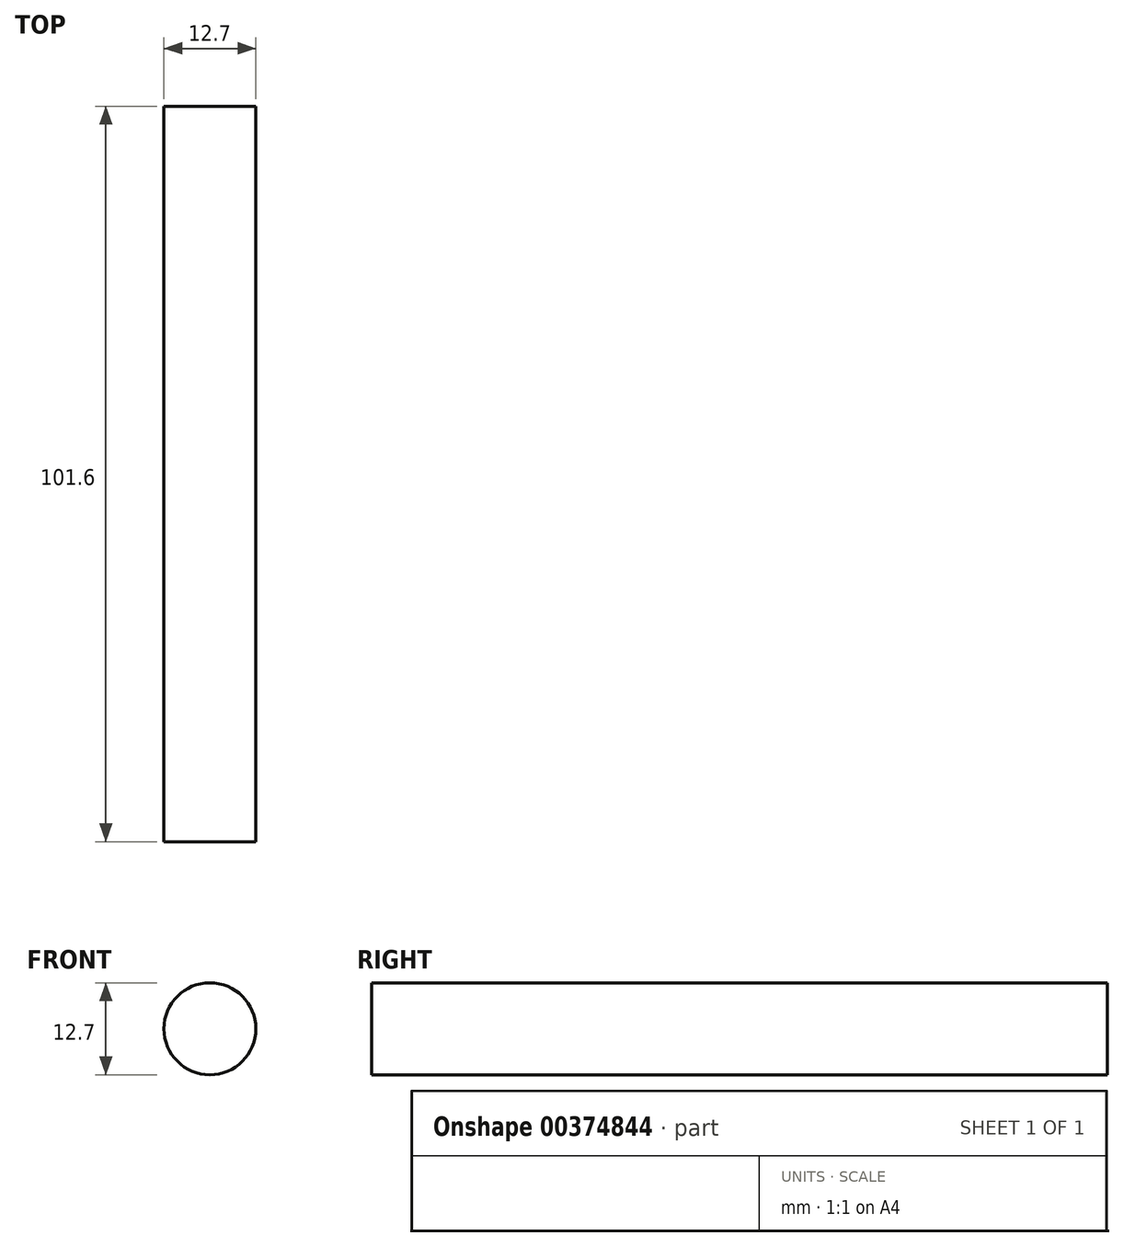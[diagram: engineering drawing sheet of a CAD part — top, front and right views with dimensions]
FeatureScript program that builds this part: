
annotation { "Feature Type Name" : "Feature", "Feature Type Description" : "" }
export const myFeature = defineFeature(function(context is Context, id is Id, definition is map)
    precondition{}
    {
        {
            var Q0;
            Q0=qCreatedBy(makeId("Front.planeOp"),FACE);
            var sketch = newSketch(context, id + "F0", { "sketchPlane" : qUnion([Q0])});
            skCircle(sketch, "E0", {"center": v(0, 0) * mm, "radius": 6.35 * mm});
            skSolve(sketch);
        }
        {
            var Q0;
            Q0=makeQuery(id+"F0.imprint","IMPRINT",FACE,{"disambiguationData":[TD([[makeQuery(id+"F0.imprint","IMPRINT",EDGE,{"derivedFrom":sQuery(id+"F0.wireOp",EDGE,"E0")}),1.0]])]});
            extrude(context, id + "F1", {"entities" : qUnion([Q0]), "depth" : 101.6 * mm});
        }
    });
